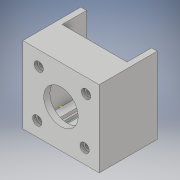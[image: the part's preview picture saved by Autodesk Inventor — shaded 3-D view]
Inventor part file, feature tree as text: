
AUTODESK INVENTOR PART (.ipt)
format: ipt  version: 2017 (Build 210142000, 142)  size: 214,528 bytes
history: native  units: in
note: dims shown in document units (in); Inventor stores cm internally (conversion verified against a paired STEP export)
features: sketch x13, extrude x8
ambient origin geometry x8: Origin, YZ Plane, XZ Plane, XY Plane, X Axis, Y Axis, Z Axis, Center Point
bodies: Solid1 (feature_tree)
feature tree (21):
  sketch  "Sketch1"  dims[d0=1.9685in d1=1.9685in]
  extrude  "Extrusion1"  Depth=1.9685in
  sketch  "Sketch3"  dims[d4=1.4961in d5=0.0in d6=1.6732in]
  extrude  "Extrusion2"  Depth=0.9843in
  extrude  "Extrusion3"  Depth=1.6732in
  sketch  "Sketch6"  dims[d12=0.7087in d13=0.0in d14=0.8858in]
  extrude  "Extrusion4"  Depth=0.1476in
  extrude  "Extrusion5"  Depth=0.1476in
  sketch  "Sketch9"  dims[d20=0.128in]
  extrude  "Extrusion6"  Depth=0.7087in
  sketch  "Sketch11"  dims[d22=1.2205in]
  extrude  "Extrusion7"  Depth=0.128in
  extrude  "Extrusion8"  Depth=0.128in
  sketch  "Sketch2"  dims[d2=0.9843in d3=0.9843in]
  sketch  "Sketch4"  dims[d7=0.6299in d8=0.1476in]
  sketch  "Sketch5"  dims[d9=1.8209in d10=0.0in d11=0.1476in]
  sketch  "Sketch7"  dims[d15=0.2362in d16=0.0in d17=0.128in]
  sketch  "Sketch8"  dims[d18=0.128in d19=0.128in]
  sketch  "Sketch10"  dims[d21=0.6102in]
  sketch  "Sketch12"  dims[d23=1.2205in]
  sketch  "Sketch13"  dims[d24=0.6102in d25=1.2205in d26=0.6102in d27=0.6102in d28=0.1575in d29=0.0in d30=0.128in d31=0.128in d32=0.6693in d33=0.6693in d34=0.9843in d35=0.4921in d36=0.1575in d37=0.0in d38=0.2362in d39=0.2362in d40=0.2362in d41=0.2362in d42=0.0787in d43=0.0in d44=0.2362in d45=0.2362in d46=0.0787in d47=0.0in]
